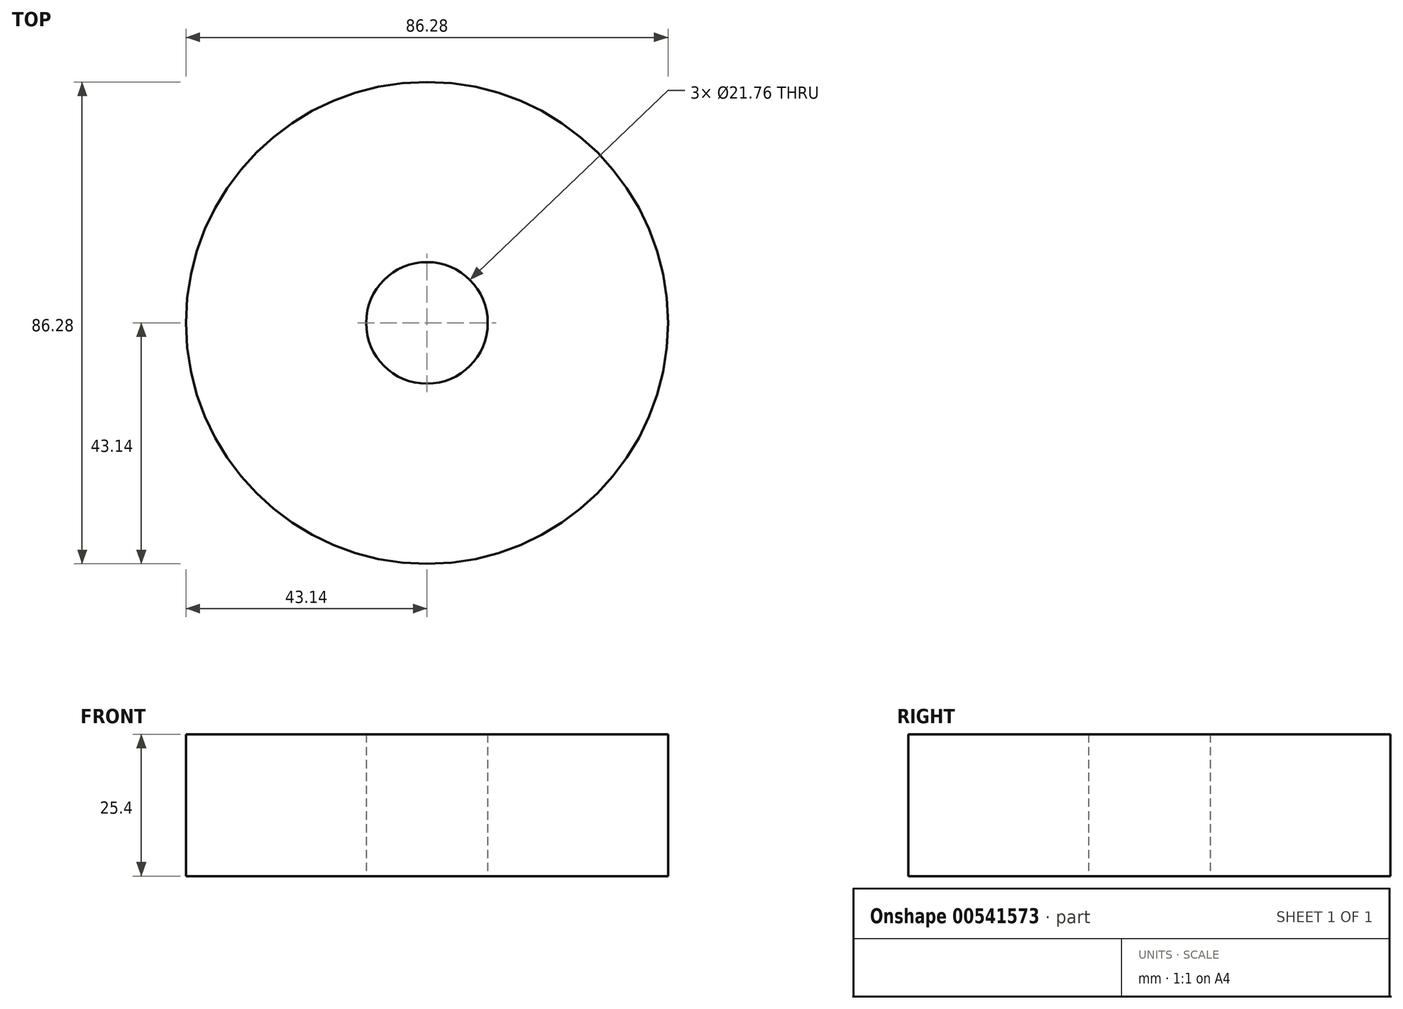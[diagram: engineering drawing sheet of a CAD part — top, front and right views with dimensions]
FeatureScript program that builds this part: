
annotation { "Feature Type Name" : "Feature", "Feature Type Description" : "" }
export const myFeature = defineFeature(function(context is Context, id is Id, definition is map)
    precondition{}
    {
        {
            var Q0;
            Q0=qCreatedBy(makeId("Top.planeOp"),FACE);
            var sketch = newSketch(context, id + "F0", { "sketchPlane" : qUnion([Q0])});
            skCircle(sketch, "E0", {"center": v(0, 0) * mm, "radius": 43.14 * mm});
            skCircle(sketch, "E1", {"center": v(0, 0) * mm, "radius": 10.88 * mm});
            skLineSegment(sketch, "E2", {"start": v(0, 0) * mm, "end": v(0, 29.96) * mm});
            skLineSegment(sketch, "E3", {"start": v(0, 29.96) * mm, "end": v(0, 0) * mm});
            skLineSegment(sketch, "E4", {"start": v(0, 0) * mm, "end": v(-21.07, -19.52) * mm});
            skLineSegment(sketch, "E5", {"start": v(-21.07, -19.52) * mm, "end": v(0, 0) * mm});
            skLineSegment(sketch, "E6", {"start": v(0, 0) * mm, "end": v(18.09, -19.52) * mm});
            skSolve(sketch);
        }
        {
            var Q0;
            Q0 = qSketchRegion(id + "F0", true);
            extrude(context, id + "F1", {"entities" : qUnion([Q0]), "depth" : 25.4 * mm, "offsetDistance" : 25.4 * mm});
        }
    });
